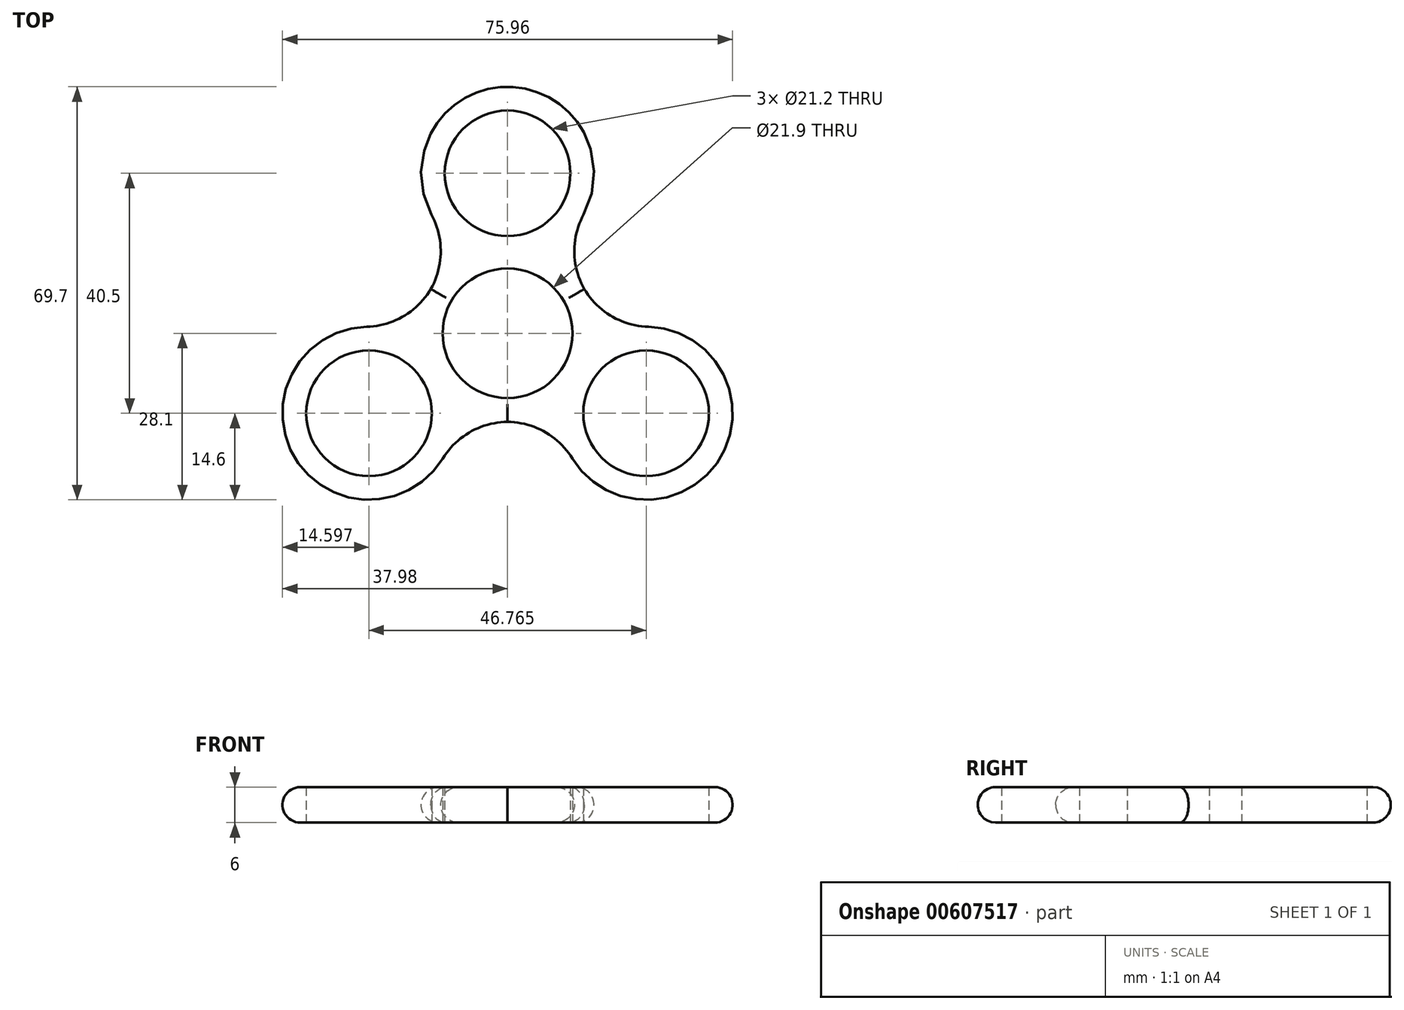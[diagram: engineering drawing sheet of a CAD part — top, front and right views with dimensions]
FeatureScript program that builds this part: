
annotation { "Feature Type Name" : "Feature", "Feature Type Description" : "" }
export const myFeature = defineFeature(function(context is Context, id is Id, definition is map)
    precondition{}
    {
        {
            var Q0;
            Q0=qCreatedBy(makeId("Top.planeOp"),FACE);
            var sketch = newSketch(context, id + "F0", { "sketchPlane" : qUnion([Q0])});
            skCircle(sketch, "E0", {"center": v(0, 0) * mm, "radius": 10.95 * mm});
            skCircle(sketch, "E1.cCircle", {"center": v(0, 0) * mm, "radius": 13.5 * mm, "construction": true});
            skLineSegment(sketch, "E1.0", {"start": v(-23.38, -13.5) * mm, "end": v(0, 27) * mm, "construction": true});
            skLineSegment(sketch, "E1.1", {"start": v(0, 27) * mm, "end": v(23.38, -13.5) * mm, "construction": true});
            skLineSegment(sketch, "E1.2", {"start": v(23.38, -13.5) * mm, "end": v(-23.38, -13.5) * mm, "construction": true});
            skPoint(sketch, "E1.0.midPoint", {"position": v(-11.7, 6.75) * mm});
            skCircle(sketch, "E2", {"center": v(0, 27) * mm, "radius": 10.6 * mm});
            skCircle(sketch, "E3", {"center": v(23.38, -13.5) * mm, "radius": 10.6 * mm});
            skCircle(sketch, "E4", {"center": v(-23.38, -13.5) * mm, "radius": 10.6 * mm});
            skCircle(sketch, "E5.0", {"center": v(-23.38, -13.5) * mm, "radius": 14.6 * mm});
            skCircle(sketch, "E6.0", {"center": v(23.38, -13.5) * mm, "radius": 14.6 * mm});
            skCircle(sketch, "E7.0", {"center": v(0, 27) * mm, "radius": 14.6 * mm});
            skCircle(sketch, "E8.0", {"center": v(0, 0) * mm, "radius": 14.95 * mm});
            skSolve(sketch);
        }
        {
            var Q0;
            Q0 = qSketchRegion(id + "F0", true);
            extrude(context, id + "F1", {"entities" : qUnion([Q0]), "depth" : 6 * mm, "offsetDistance" : 25 * mm});
        }
        {
            var Q0;
            {var subQ0=sQuery(id+"F0.wireOp",EDGE,"E8.0");var subQ1=sQuery(id+"F0.wireOp",EDGE,"E5.0");Q0=makeQuery(id+"F1.opExtrude","SWEPT_EDGE",EDGE,{"disambiguationData":[OSD([subQ1,subQ0]),TDD([makeQuery(id+"F0.imprint","INTERSECT",VERTEX,{"disambiguationData":[OD(1.0)],"derivedFrom":[subQ1,subQ0]})])]});}
            var Q1;
            {var subQ0=sQuery(id+"F0.wireOp",EDGE,"E8.0");var subQ1=sQuery(id+"F0.wireOp",EDGE,"E6.0");Q1=makeQuery(id+"F1.opExtrude","SWEPT_EDGE",EDGE,{"disambiguationData":[OSD([subQ1,subQ0]),TDD([makeQuery(id+"F0.imprint","INTERSECT",VERTEX,{"disambiguationData":[OD(0.0)],"derivedFrom":[subQ1,subQ0]})])]});}
            var Q2;
            {var subQ0=sQuery(id+"F0.wireOp",EDGE,"E8.0");var subQ1=sQuery(id+"F0.wireOp",EDGE,"E7.0");Q2=makeQuery(id+"F1.opExtrude","SWEPT_EDGE",EDGE,{"disambiguationData":[OSD([subQ1,subQ0]),TDD([makeQuery(id+"F0.imprint","INTERSECT",VERTEX,{"disambiguationData":[OD(1.0)],"derivedFrom":[subQ1,subQ0]})])]});}
            var Q3;
            {var subQ0=sQuery(id+"F0.wireOp",EDGE,"E8.0");var subQ1=sQuery(id+"F0.wireOp",EDGE,"E6.0");Q3=makeQuery(id+"F1.opExtrude","SWEPT_EDGE",EDGE,{"disambiguationData":[OSD([subQ1,subQ0]),TDD([makeQuery(id+"F0.imprint","INTERSECT",VERTEX,{"disambiguationData":[OD(1.0)],"derivedFrom":[subQ1,subQ0]})])]});}
            var Q4;
            {var subQ0=sQuery(id+"F0.wireOp",EDGE,"E8.0");var subQ1=sQuery(id+"F0.wireOp",EDGE,"E7.0");Q4=makeQuery(id+"F1.opExtrude","SWEPT_EDGE",EDGE,{"disambiguationData":[OSD([subQ1,subQ0]),TDD([makeQuery(id+"F0.imprint","INTERSECT",VERTEX,{"disambiguationData":[OD(0.0)],"derivedFrom":[subQ1,subQ0]})])]});}
            var Q5;
            {var subQ0=sQuery(id+"F0.wireOp",EDGE,"E8.0");var subQ1=sQuery(id+"F0.wireOp",EDGE,"E5.0");Q5=makeQuery(id+"F1.opExtrude","SWEPT_EDGE",EDGE,{"disambiguationData":[OSD([subQ1,subQ0]),TDD([makeQuery(id+"F0.imprint","INTERSECT",VERTEX,{"disambiguationData":[OD(0.0)],"derivedFrom":[subQ1,subQ0]})])]});}
            fillet(context, id + "F2", {"entities" : qUnion([Q0, Q1, Q2, Q3, Q4, Q5]), "radius" : 13 * mm, "tangentPropagation" : true, "allowEdgeOverflow" : false});
        }
        {
            var Q0;
            Q0=makeQuery(id+"F1.opExtrude","CAP_EDGE",EDGE,{"disambiguationData":[OSD([sQuery(id+"F0.wireOp",EDGE,"E7.0")])],"isStart":false});
            var Q1;
            Q1=makeQuery(id+"F1.opExtrude","CAP_EDGE",EDGE,{"disambiguationData":[OSD([sQuery(id+"F0.wireOp",EDGE,"E7.0")])],"isStart":true});
            var Q2;
            Q2=makeQuery(id+"F1.opExtrude","CAP_EDGE",EDGE,{"disambiguationData":[OSD([sQuery(id+"F0.wireOp",EDGE,"E5.0")])],"isStart":false});
            var Q3;
            Q3=makeQuery(id+"F1.opExtrude","CAP_EDGE",EDGE,{"disambiguationData":[OSD([sQuery(id+"F0.wireOp",EDGE,"E5.0")])],"isStart":true});
            var Q4;
            Q4=makeQuery(id+"F1.opExtrude","CAP_EDGE",EDGE,{"disambiguationData":[OSD([sQuery(id+"F0.wireOp",EDGE,"E6.0")])],"isStart":false});
            var Q5;
            Q5=makeQuery(id+"F1.opExtrude","CAP_EDGE",EDGE,{"disambiguationData":[OSD([sQuery(id+"F0.wireOp",EDGE,"E6.0")])],"isStart":true});
            fillet(context, id + "F3", {"entities" : qUnion([Q0, Q1, Q2, Q3, Q4, Q5]), "radius" : 3 * mm, "tangentPropagation" : true, "allowEdgeOverflow" : false});
        }
    });
